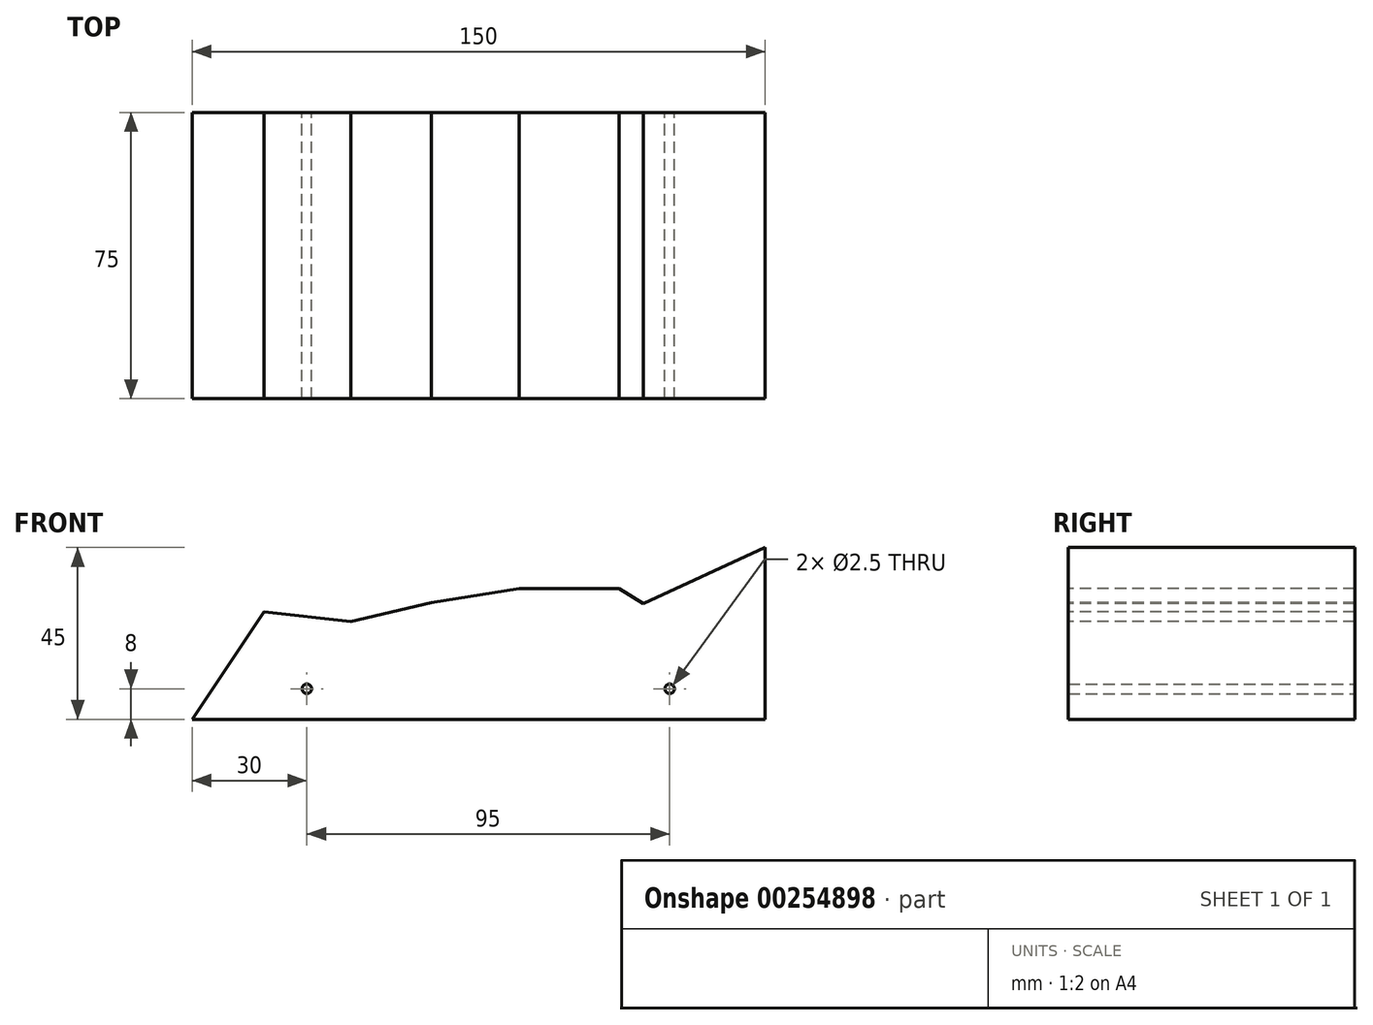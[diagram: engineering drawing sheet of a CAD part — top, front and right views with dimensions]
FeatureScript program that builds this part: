
annotation { "Feature Type Name" : "Feature", "Feature Type Description" : "" }
export const myFeature = defineFeature(function(context is Context, id is Id, definition is map)
    precondition{}
    {
        {
            var Q0;
            Q0=qCreatedBy(makeId("Front.planeOp"),FACE);
            var sketch = newSketch(context, id + "F0", { "sketchPlane" : qUnion([Q0])});
            skLineSegment(sketch, "E0.bottom", {"start": v(-60, 22.5) * mm, "end": v(60, 22.5) * mm});
            skLineSegment(sketch, "E0.top", {"start": v(-60, -22.5) * mm, "end": v(60, -22.5) * mm});
            skLineSegment(sketch, "E0.right", {"start": v(60, 22.5) * mm, "end": v(60, -22.5) * mm});
            skPoint(sketch, "E0.middle", {"position": v(0, 0) * mm});
            skLineSegment(sketch, "E1", {"start": v(-60, -22.5) * mm, "end": v(-90, -22.5) * mm});
            skLineSegment(sketch, "E2", {"start": v(-60, 22.5) * mm, "end": v(-90, -22.5) * mm});
            skLineSegment(sketch, "E3", {"start": v(60, -22.5) * mm, "end": v(35, -22.5) * mm});
            skLineSegment(sketch, "E4", {"start": v(35, -15.75) * mm, "end": v(35, -14.5) * mm});
            skLineSegment(sketch, "E5", {"start": v(-60, -15.75) * mm, "end": v(-60, -14.5) * mm});
            skCircle(sketch, "E6", {"center": v(-60, -14.5) * mm, "radius": 1.25 * mm});
            skCircle(sketch, "E7", {"center": v(35, -14.5) * mm, "radius": 1.25 * mm});
            skSolve(sketch);
        }
        {
            var Q0;
            Q0=makeQuery(id+"F0.imprint","IMPRINT",FACE,{"disambiguationData":[TD([[makeQuery(id+"F0.imprint","IMPRINT",EDGE,{"derivedFrom":sQuery(id+"F0.wireOp",EDGE,"E0.bottom")}),-1.0]])]});
            extrude(context, id + "F1", {"entities" : qUnion([Q0]), "depth" : 25 * mm});
        }
        {
            var Q0;
            Q0=makeQuery(id+"F0.imprint","IMPRINT",FACE,{"disambiguationData":[TD([[makeQuery(id+"F0.imprint","IMPRINT",EDGE,{"derivedFrom":sQuery(id+"F0.wireOp",EDGE,"E0.bottom")}),-1.0]])]});
            extrude(context, id + "F2", {"entities" : qUnion([Q0]), "operationType" : NewBodyOperationType.ADD, "depth" : 50 * mm});
        }
        {
            var Q0;
            Q0=makeQuery(id+"F0.imprint","IMPRINT",FACE,{"disambiguationData":[TD([[makeQuery(id+"F0.imprint","IMPRINT",EDGE,{"derivedFrom":sQuery(id+"F0.wireOp",EDGE,"E0.bottom")}),-1.0]])]});
            extrude(context, id + "F3", {"entities" : qUnion([Q0]), "operationType" : NewBodyOperationType.ADD, "depth" : 25 * mm});
        }
        {
            var Q0;
            Q0=makeQuery(id+"F2.opExtrude","CAP_FACE",FACE,{"disambiguationData":[OSD([sQuery(id+"F0.wireOp",EDGE,"E0.bottom"),sQuery(id+"F0.wireOp",EDGE,"E0.top"),sQuery(id+"F0.wireOp",EDGE,"E0.right"),sQuery(id+"F0.wireOp",EDGE,"E1"),sQuery(id+"F0.wireOp",EDGE,"E2"),sQuery(id+"F0.wireOp",EDGE,"E3"),sQuery(id+"F0.wireOp",EDGE,"E6"),sQuery(id+"F0.wireOp",EDGE,"E7")])],"isStart":false});
            var sketch = newSketch(context, id + "F4", { "sketchPlane" : qUnion([Q0])});
            skLineSegment(sketch, "E8", {"start": v(-71.23, 5.65) * mm, "end": v(-48.47, 3.14) * mm});
            skLineSegment(sketch, "E9", {"start": v(-48.47, 3.14) * mm, "end": v(-27.44, 8.04) * mm});
            skLineSegment(sketch, "E10", {"start": v(-27.44, 8.04) * mm, "end": v(-4.37, 11.71) * mm});
            skLineSegment(sketch, "E11", {"start": v(-4.37, 11.71) * mm, "end": v(21.76, 11.71) * mm});
            skLineSegment(sketch, "E12", {"start": v(21.76, 11.71) * mm, "end": v(28.09, 7.83) * mm});
            skLineSegment(sketch, "E13", {"start": v(28.09, 7.83) * mm, "end": v(60, 22.5) * mm});
            skSolve(sketch);
        }
        {
            var Q0;
            {var subQ0=sQuery(id+"F4.wireOp",EDGE,"E8");Q0=makeQuery(id+"F4.imprint","IMPRINT",FACE,{"disambiguationData":[TD([[makeQuery(id+"F4.imprint","IMPRINT",EDGE,{"derivedFrom":subQ0}),1.0]])]});}
            extrude(context, id + "F5", {"entities" : qUnion([Q0]), "operationType" : NewBodyOperationType.REMOVE, "oppositeDirection" : true, "depth" : 25 * mm});
        }
        {
            var Q0;
            {var subQ0=sQuery(id+"F4.wireOp",EDGE,"E8");Q0=makeQuery(id+"F4.imprint","IMPRINT",FACE,{"disambiguationData":[TD([[makeQuery(id+"F4.imprint","IMPRINT",EDGE,{"derivedFrom":subQ0}),1.0]])]});}
            extrude(context, id + "F6", {"entities" : qUnion([Q0]), "operationType" : NewBodyOperationType.REMOVE, "endBound" : BoundingType.THROUGH_ALL, "oppositeDirection" : true, "depth" : 25 * mm});
        }
        {
            var Q0;
            Q0=makeQuery(id+"F2.opExtrude","CAP_FACE",FACE,{"disambiguationData":[OSD([sQuery(id+"F0.wireOp",EDGE,"E0.bottom"),sQuery(id+"F0.wireOp",EDGE,"E0.top"),sQuery(id+"F0.wireOp",EDGE,"E0.right"),sQuery(id+"F0.wireOp",EDGE,"E1"),sQuery(id+"F0.wireOp",EDGE,"E2"),sQuery(id+"F0.wireOp",EDGE,"E3"),sQuery(id+"F0.wireOp",EDGE,"E6"),sQuery(id+"F0.wireOp",EDGE,"E7")])],"isStart":false});
            extrude(context, id + "F7", {"entities" : qUnion([Q0]), "operationType" : NewBodyOperationType.ADD, "depth" : 25 * mm});
        }
    });
